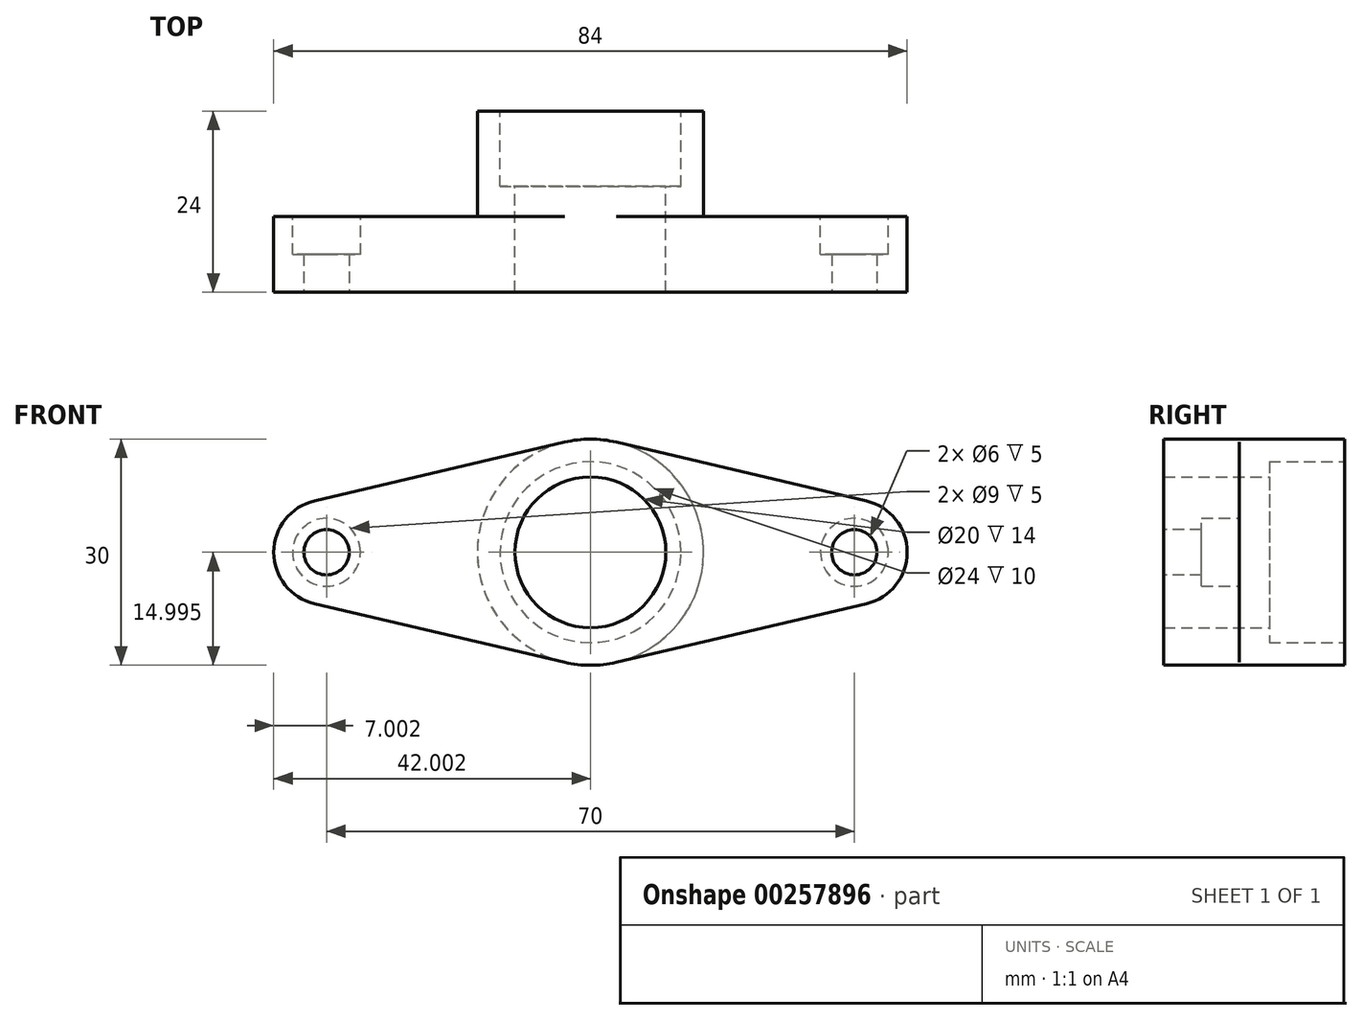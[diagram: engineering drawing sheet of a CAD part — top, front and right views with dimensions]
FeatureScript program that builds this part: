
annotation { "Feature Type Name" : "Feature", "Feature Type Description" : "" }
export const myFeature = defineFeature(function(context is Context, id is Id, definition is map)
    precondition{}
    {
        {
            var Q0;
            Q0=qCreatedBy(makeId("Front.planeOp"),FACE);
            var sketch = newSketch(context, id + "F0", { "sketchPlane" : qUnion([Q0])});
            skLineSegment(sketch, "E0", {"start": v(-39.45, 14.33) * mm, "end": v(30.55, 14.33) * mm, "construction": true});
            skArc(sketch, "E1", {"start": v(-1.02, 28.93) * mm, "mid": v(-4.45, 29.33) * mm, "end": v(-7.88, 28.93) * mm});
            skArc(sketch, "E2", {"start": v(-41.05, 21.14) * mm, "mid": v(-46.45, 14.33) * mm, "end": v(-41.05, 7.51) * mm});
            skArc(sketch, "E3", {"start": v(32.15, 7.51) * mm, "mid": v(37.55, 14.33) * mm, "end": v(32.15, 21.14) * mm});
            skLineSegment(sketch, "E4", {"start": v(-41.05, 21.14) * mm, "end": v(-7.88, 28.93) * mm});
            skLineSegment(sketch, "E5", {"start": v(-41.05, 7.51) * mm, "end": v(-7.88, -0.28) * mm});
            skLineSegment(sketch, "E6", {"start": v(32.15, 7.51) * mm, "end": v(-1.02, -0.28) * mm});
            skLineSegment(sketch, "E7", {"start": v(-1.02, 28.93) * mm, "end": v(32.15, 21.14) * mm});
            skArc(sketch, "E8.trimOffspring", {"start": v(-7.88, -0.28) * mm, "mid": v(-4.45, -0.67) * mm, "end": v(-1.02, -0.28) * mm});
            skSolve(sketch);
        }
        {
            var Q0;
            Q0=makeQuery(id+"F0.imprint","IMPRINT",FACE,{"disambiguationData":[TD([[makeQuery(id+"F0.imprint","IMPRINT",EDGE,{"derivedFrom":sQuery(id+"F0.wireOp",EDGE,"E1")}),1.0]])]});
            extrude(context, id + "F1", {"entities" : qUnion([Q0]), "depth" : 10 * mm});
        }
        {
            var Q0;
            Q0=makeQuery(id+"F1.opExtrude","CAP_FACE",FACE,{"disambiguationData":[OSD([sQuery(id+"F0.wireOp",EDGE,"E1"),sQuery(id+"F0.wireOp",EDGE,"E2"),sQuery(id+"F0.wireOp",EDGE,"E3"),sQuery(id+"F0.wireOp",EDGE,"E4"),sQuery(id+"F0.wireOp",EDGE,"E5"),sQuery(id+"F0.wireOp",EDGE,"E6"),sQuery(id+"F0.wireOp",EDGE,"E7"),sQuery(id+"F0.wireOp",EDGE,"E8.trimOffspring")])],"isStart":false});
            var sketch = newSketch(context, id + "F2", { "sketchPlane" : qUnion([Q0])});
            skCircle(sketch, "E9", {"center": v(-39.45, 14.33) * mm, "radius": 4.5 * mm});
            skCircle(sketch, "E10", {"center": v(30.55, 14.33) * mm, "radius": 4.5 * mm});
            skCircle(sketch, "E11", {"center": v(-39.45, 14.33) * mm, "radius": 3 * mm});
            skCircle(sketch, "E12", {"center": v(30.55, 14.33) * mm, "radius": 3 * mm});
            skSolve(sketch);
        }
        {
            var Q0;
            Q0=makeQuery(id+"F2.imprint","IMPRINT",FACE,{"disambiguationData":[TD([[makeQuery(id+"F2.imprint","IMPRINT",EDGE,{"derivedFrom":sQuery(id+"F2.wireOp",EDGE,"E11")}),1.0]])]});
            var Q1;
            Q1=makeQuery(id+"F2.imprint","IMPRINT",FACE,{"disambiguationData":[TD([[makeQuery(id+"F2.imprint","IMPRINT",EDGE,{"derivedFrom":sQuery(id+"F2.wireOp",EDGE,"E12")}),1.0]])]});
            extrude(context, id + "F3", {"entities" : qUnion([Q0, Q1]), "operationType" : NewBodyOperationType.REMOVE, "oppositeDirection" : true, "depth" : 10 * mm});
        }
        {
            var Q0;
            Q0=makeQuery(id+"F1.opExtrude","CAP_FACE",FACE,{"disambiguationData":[OSD([sQuery(id+"F0.wireOp",EDGE,"E1"),sQuery(id+"F0.wireOp",EDGE,"E2"),sQuery(id+"F0.wireOp",EDGE,"E3"),sQuery(id+"F0.wireOp",EDGE,"E4"),sQuery(id+"F0.wireOp",EDGE,"E5"),sQuery(id+"F0.wireOp",EDGE,"E6"),sQuery(id+"F0.wireOp",EDGE,"E7"),sQuery(id+"F0.wireOp",EDGE,"E8.trimOffspring")])],"isStart":false});
            var sketch = newSketch(context, id + "F4", { "sketchPlane" : qUnion([Q0])});
            skCircle(sketch, "E13", {"center": v(-39.45, 14.33) * mm, "radius": 4.5 * mm});
            skCircle(sketch, "E14", {"center": v(30.55, 14.33) * mm, "radius": 4.5 * mm});
            skSolve(sketch);
        }
        {
            var Q0;
            Q0=makeQuery(id+"F4.imprint","IMPRINT",FACE,{"disambiguationData":[TD([[makeQuery(id+"F4.imprint","IMPRINT",EDGE,{"derivedFrom":sQuery(id+"F4.wireOp",EDGE,"E13")}),1.0]])]});
            var Q1;
            Q1=makeQuery(id+"F4.imprint","IMPRINT",FACE,{"disambiguationData":[TD([[makeQuery(id+"F4.imprint","IMPRINT",EDGE,{"derivedFrom":sQuery(id+"F4.wireOp",EDGE,"E14")}),1.0]])]});
            extrude(context, id + "F5", {"entities" : qUnion([Q0, Q1]), "operationType" : NewBodyOperationType.ADD, "oppositeDirection" : true, "depth" : 5 * mm});
        }
        {
            var Q0;
            Q0=qCreatedBy(makeId("Front.planeOp"),FACE);
            var sketch = newSketch(context, id + "F6", { "sketchPlane" : qUnion([Q0])});
            skCircle(sketch, "E15", {"center": v(-39.45, 14.33) * mm, "radius": 4.5 * mm});
            skCircle(sketch, "E16", {"center": v(30.55, 14.33) * mm, "radius": 4.5 * mm});
            skSolve(sketch);
        }
        {
            var Q0;
            Q0=makeQuery(id+"F6.imprint","IMPRINT",FACE,{"disambiguationData":[TD([[makeQuery(id+"F6.imprint","IMPRINT",EDGE,{"derivedFrom":sQuery(id+"F6.wireOp",EDGE,"E15")}),1.0]])]});
            extrude(context, id + "F7", {"entities" : qUnion([Q0]), "operationType" : NewBodyOperationType.REMOVE, "oppositeDirection" : true, "depth" : 5 * mm});
        }
        {
            var Q0;
            Q0 = qSketchRegion(id + "F6", true);
            extrude(context, id + "F8", {"entities" : qUnion([Q0]), "operationType" : NewBodyOperationType.REMOVE, "depth" : 5 * mm});
        }
        {
            var Q0;
            Q0=makeQuery(id+"F1.opExtrude","CAP_FACE",FACE,{"disambiguationData":[OSD([sQuery(id+"F0.wireOp",EDGE,"E1"),sQuery(id+"F0.wireOp",EDGE,"E2"),sQuery(id+"F0.wireOp",EDGE,"E3"),sQuery(id+"F0.wireOp",EDGE,"E4"),sQuery(id+"F0.wireOp",EDGE,"E5"),sQuery(id+"F0.wireOp",EDGE,"E6"),sQuery(id+"F0.wireOp",EDGE,"E7"),sQuery(id+"F0.wireOp",EDGE,"E8.trimOffspring")])],"isStart":true});
            var sketch = newSketch(context, id + "F9", { "sketchPlane" : qUnion([Q0])});
            skCircle(sketch, "E17", {"center": v(4.45, 14.33) * mm, "radius": 15 * mm});
            skSolve(sketch);
        }
        {
            var Q0;
            {var subQ0=sQuery(id+"F9.wireOp",EDGE,"E17");var subQ1=makeQuery(id+"F9.imprint","INTERSECT",VERTEX,{"derivedFrom":[makeQuery(id+"F1.opExtrude","CAP_EDGE",EDGE,{"disambiguationData":[OSD([sQuery(id+"F0.wireOp",EDGE,"E7")])],"isStart":true}),subQ0]});var subQ2=makeQuery(id+"F9.imprint","INTERSECT",VERTEX,{"derivedFrom":[makeQuery(id+"F1.opExtrude","CAP_EDGE",EDGE,{"disambiguationData":[OSD([sQuery(id+"F0.wireOp",EDGE,"E4")])],"isStart":true}),subQ0]});Q0=makeQuery(id+"F9.imprint","IMPRINT",FACE,{"disambiguationData":[TD([[makeQuery(id+"F9.imprint","IMPRINT",EDGE,{"disambiguationData":[TD([[subQ1,-1.0],[subQ2,1.0]])],"derivedFrom":subQ0}),-1.0]])]});}
            extrude(context, id + "F10", {"entities" : qUnion([Q0]), "operationType" : NewBodyOperationType.ADD, "depth" : 14 * mm});
        }
        {
            var Q0;
            Q0=makeQuery(id+"F10.opExtrude","CAP_FACE",FACE,{"disambiguationData":[OSD([sQuery(id+"F9.wireOp",EDGE,"E17")])],"isStart":false});
            var sketch = newSketch(context, id + "F11", { "sketchPlane" : qUnion([Q0])});
            skCircle(sketch, "E18", {"center": v(4.45, 14.33) * mm, "radius": 12 * mm});
            skCircle(sketch, "E19", {"center": v(4.45, 14.33) * mm, "radius": 10 * mm});
            skSolve(sketch);
        }
        {
            var Q0;
            Q0=makeQuery(id+"F11.imprint","IMPRINT",FACE,{"disambiguationData":[TD([[makeQuery(id+"F11.imprint","IMPRINT",EDGE,{"derivedFrom":sQuery(id+"F11.wireOp",EDGE,"E19")}),1.0]])]});
            extrude(context, id + "F12", {"entities" : qUnion([Q0]), "operationType" : NewBodyOperationType.REMOVE, "depth" : 20 * mm});
        }
        {
            var Q0;
            Q0=makeQuery(id+"F10.opExtrude","CAP_FACE",FACE,{"disambiguationData":[OSD([sQuery(id+"F9.wireOp",EDGE,"E17")])],"isStart":false});
            var sketch = newSketch(context, id + "F13", { "sketchPlane" : qUnion([Q0])});
            skCircle(sketch, "E20", {"center": v(4.45, 14.33) * mm, "radius": 10 * mm});
            skSolve(sketch);
        }
        {
            var Q0;
            Q0=makeQuery(id+"F13.imprint","IMPRINT",FACE,{"disambiguationData":[TD([[makeQuery(id+"F13.imprint","IMPRINT",EDGE,{"derivedFrom":sQuery(id+"F13.wireOp",EDGE,"E20")}),1.0]])]});
            extrude(context, id + "F14", {"entities" : qUnion([Q0]), "operationType" : NewBodyOperationType.REMOVE, "oppositeDirection" : true, "depth" : 40 * mm});
        }
        {
            var Q0;
            Q0=makeQuery(id+"F10.opExtrude","CAP_FACE",FACE,{"disambiguationData":[OSD([sQuery(id+"F9.wireOp",EDGE,"E17")])],"isStart":false});
            var sketch = newSketch(context, id + "F15", { "sketchPlane" : qUnion([Q0])});
            skCircle(sketch, "E21", {"center": v(4.45, 14.33) * mm, "radius": 12 * mm});
            skSolve(sketch);
        }
        {
            var Q0;
            Q0=makeQuery(id+"F15.imprint","IMPRINT",FACE,{"disambiguationData":[TD([[makeQuery(id+"F15.imprint","IMPRINT",EDGE,{"derivedFrom":sQuery(id+"F15.wireOp",EDGE,"E21")}),1.0]])]});
            var Q1;
            Q1=sQuery(id+"F15.wireOp",EDGE,"E21");
            extrude(context, id + "F16", {"entities" : qUnion([Q0]), "operationType" : NewBodyOperationType.REMOVE, "surfaceEntities" : qUnion([Q1]), "oppositeDirection" : true, "depth" : 10 * mm});
        }
    });
